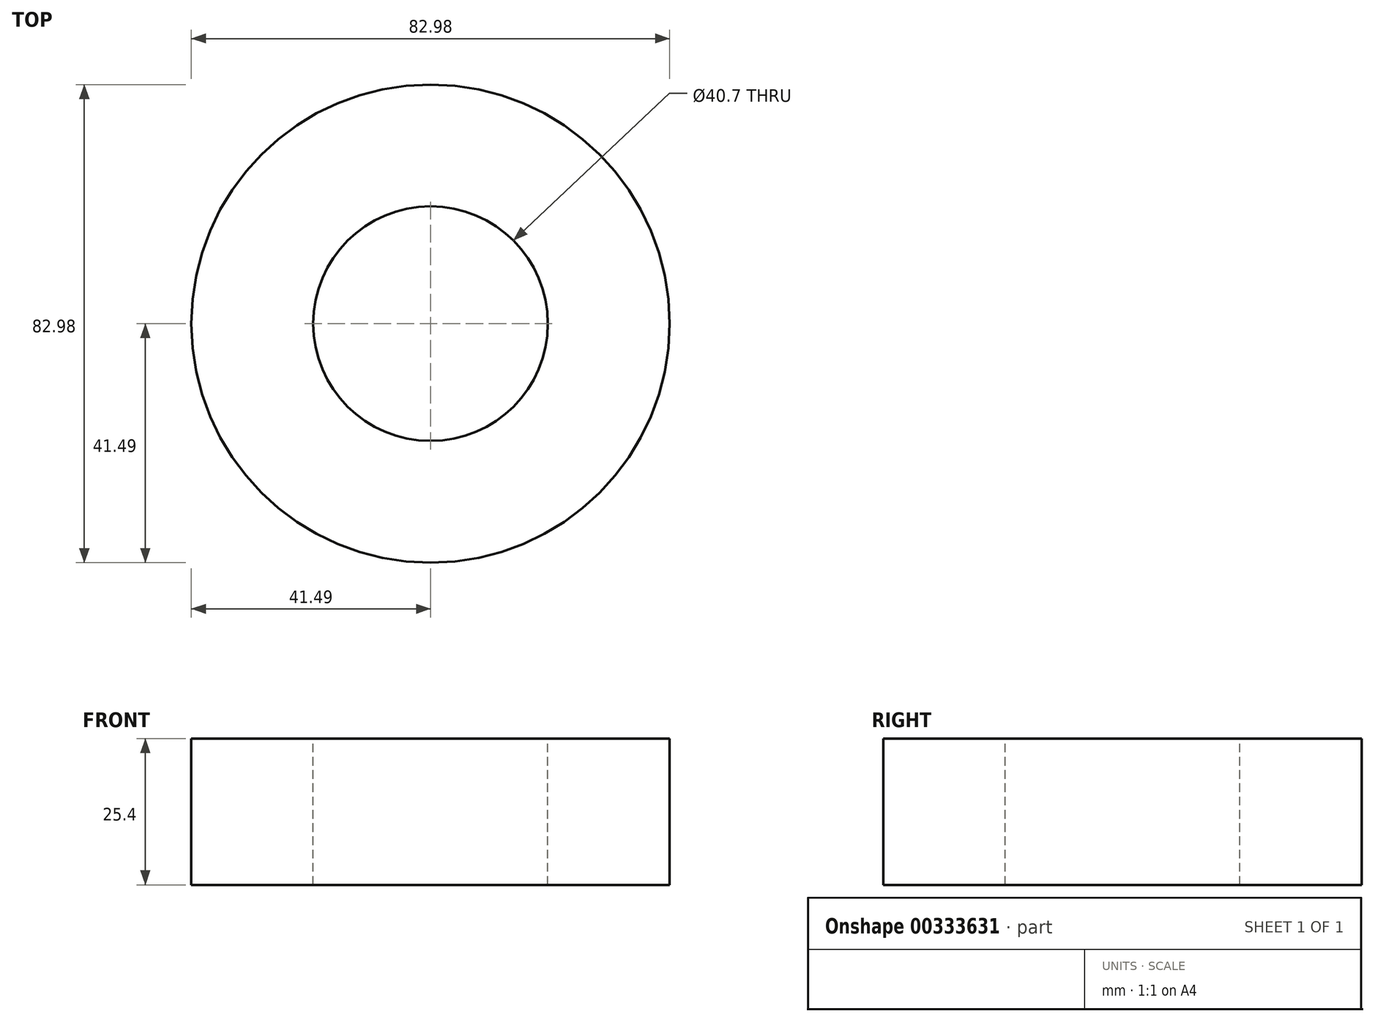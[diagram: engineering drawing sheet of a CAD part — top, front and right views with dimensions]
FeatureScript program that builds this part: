
annotation { "Feature Type Name" : "Feature", "Feature Type Description" : "" }
export const myFeature = defineFeature(function(context is Context, id is Id, definition is map)
    precondition{}
    {
        {
            var Q0;
            Q0=qCreatedBy(makeId("Top.planeOp"),FACE);
            var sketch = newSketch(context, id + "F0", { "sketchPlane" : qUnion([Q0])});
            skCircle(sketch, "E0", {"center": v(0, 0) * mm, "radius": 41.5 * mm});
            skSolve(sketch);
        }
        {
            var Q0;
            Q0 = qSketchRegion(id + "F0", true);
            extrude(context, id + "F1", {"entities" : qUnion([Q0]), "depth" : 25.4 * mm, "symmetric" : true});
        }
        {
            var Q0;
            Q0=makeQuery(id+"F1.opExtrude","CAP_FACE",FACE,{"disambiguationData":[OSD([sQuery(id+"F0.wireOp",EDGE,"E0")])],"isStart":false});
            var sketch = newSketch(context, id + "F2", { "sketchPlane" : qUnion([Q0])});
            skCircle(sketch, "E1", {"center": v(0, 0) * mm, "radius": 20.35 * mm});
            skSolve(sketch);
        }
        {
            var Q0;
            Q0 = qSketchRegion(id + "F2", true);
            extrude(context, id + "F3", {"entities" : qUnion([Q0]), "operationType" : NewBodyOperationType.REMOVE, "oppositeDirection" : true, "depth" : 25.4 * mm, "offsetDistance" : 25.4 * mm});
        }
    });
